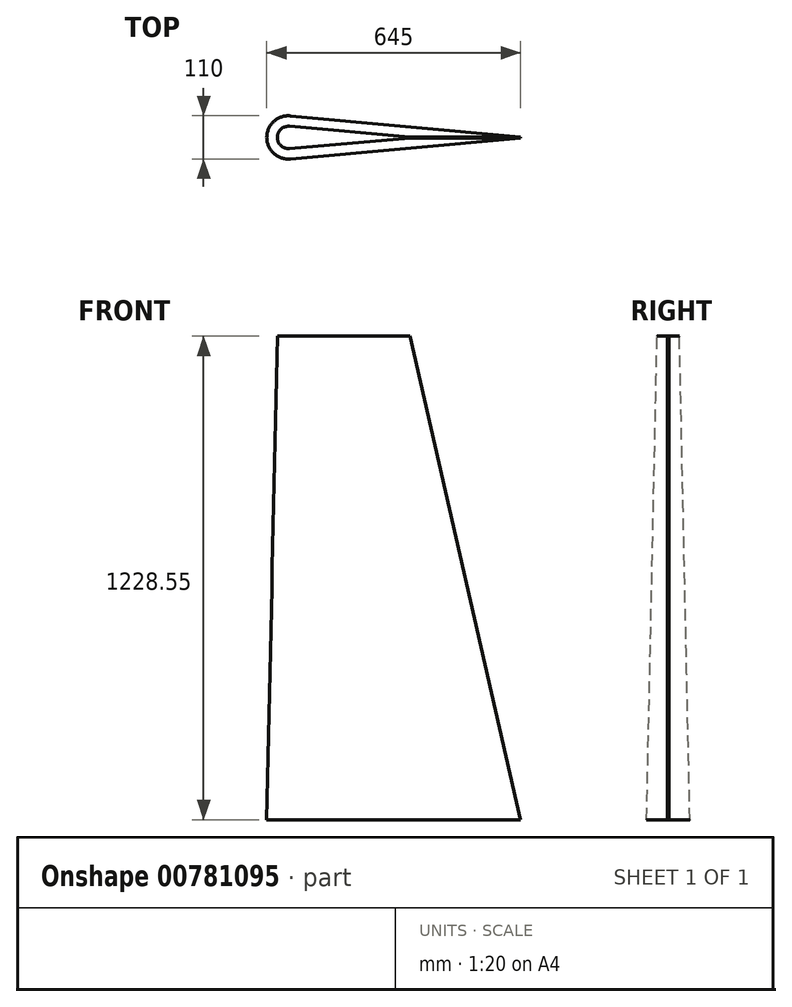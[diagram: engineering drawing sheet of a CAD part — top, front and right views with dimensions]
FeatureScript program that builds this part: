
annotation { "Feature Type Name" : "Feature", "Feature Type Description" : "" }
export const myFeature = defineFeature(function(context is Context, id is Id, definition is map)
    precondition{}
    {
        {
            var Q0;
            Q0=qCreatedBy(makeId("Top.planeOp"),FACE);
            var Q1;
            Q1 = qBodyType(qCreatedBy(id + "F2" ,EDGE), BodyType.WIRE);
            cPlane(context, id + "F0", {"entities" : qUnion([Q0, Q1]), "cplaneType" : CPlaneType.OFFSET, "offset" : 1228.55 * mm, "width" : 150 * mm, "height" : 150 * mm});
        }
        {
            var Q0;
            Q0=qCreatedBy(makeId("Top.planeOp"),FACE);
            var sketch = newSketch(context, id + "F1", { "sketchPlane" : qUnion([Q0])});
            skLineSegment(sketch, "E0", {"start": v(590, 0) * mm, "end": v(590, 1.5) * mm});
            skLineSegment(sketch, "E1", {"start": v(590, 1.5) * mm, "end": v(4.99, 54.77) * mm});
            skArc(sketch, "E2", {"start": v(4.99, 54.77) * mm, "mid": v(-37.09, 40.62) * mm, "end": v(-55, 0) * mm});
            skLineSegment(sketch, "E3.MirrorCS", {"start": v(590, -1.5) * mm, "end": v(4.99, -54.77) * mm});
            skLineSegment(sketch, "E4.MirrorCS", {"start": v(590, 0) * mm, "end": v(590, -1.5) * mm});
            skArc(sketch, "E5.MirrorCS", {"start": v(4.99, -54.77) * mm, "mid": v(-37.09, -40.62) * mm, "end": v(-55, 0) * mm});
            skSolve(sketch);
        }
        {
            var Q0;
            Q0=qCreatedBy(id+"F0.planeOp",FACE);
            var sketch = newSketch(context, id + "F2", { "sketchPlane" : qUnion([Q0])});
            skLineSegment(sketch, "E6", {"start": v(309.2, 0) * mm, "end": v(309.2, 1.5) * mm});
            skLineSegment(sketch, "E7", {"start": v(309.2, 1.5) * mm, "end": v(2.45, 28.2) * mm});
            skArc(sketch, "E8", {"start": v(2.45, 28.2) * mm, "mid": v(-19.12, 20.86) * mm, "end": v(-28.3, 0) * mm});
            skLineSegment(sketch, "E9.MirrorCS", {"start": v(309.2, -1.5) * mm, "end": v(2.45, -28.2) * mm});
            skLineSegment(sketch, "E10.MirrorCS", {"start": v(309.2, 0) * mm, "end": v(309.2, -1.5) * mm});
            skArc(sketch, "E11.MirrorCS", {"start": v(2.45, -28.2) * mm, "mid": v(-19.12, -20.86) * mm, "end": v(-28.3, 0) * mm});
            skSolve(sketch);
        }
        {
            var Q0;
            Q0=makeQuery(id+"F1.imprint","IMPRINT",FACE,{"disambiguationData":[TD([[makeQuery(id+"F1.imprint","IMPRINT",EDGE,{"derivedFrom":sQuery(id+"F1.wireOp",EDGE,"E0")}),1.0]])]});
            var Q1;
            Q1=makeQuery(id+"F2.imprint","IMPRINT",FACE,{"disambiguationData":[TD([[makeQuery(id+"F2.imprint","IMPRINT",EDGE,{"derivedFrom":sQuery(id+"F2.wireOp",EDGE,"E6")}),1.0]])]});
            loft(context, id + "F3", {"sheetProfilesArray" : [{ "sheetProfileEntities" : qUnion([Q0]) }, { "sheetProfileEntities" : qUnion([Q1]) }]});
        }
    });
